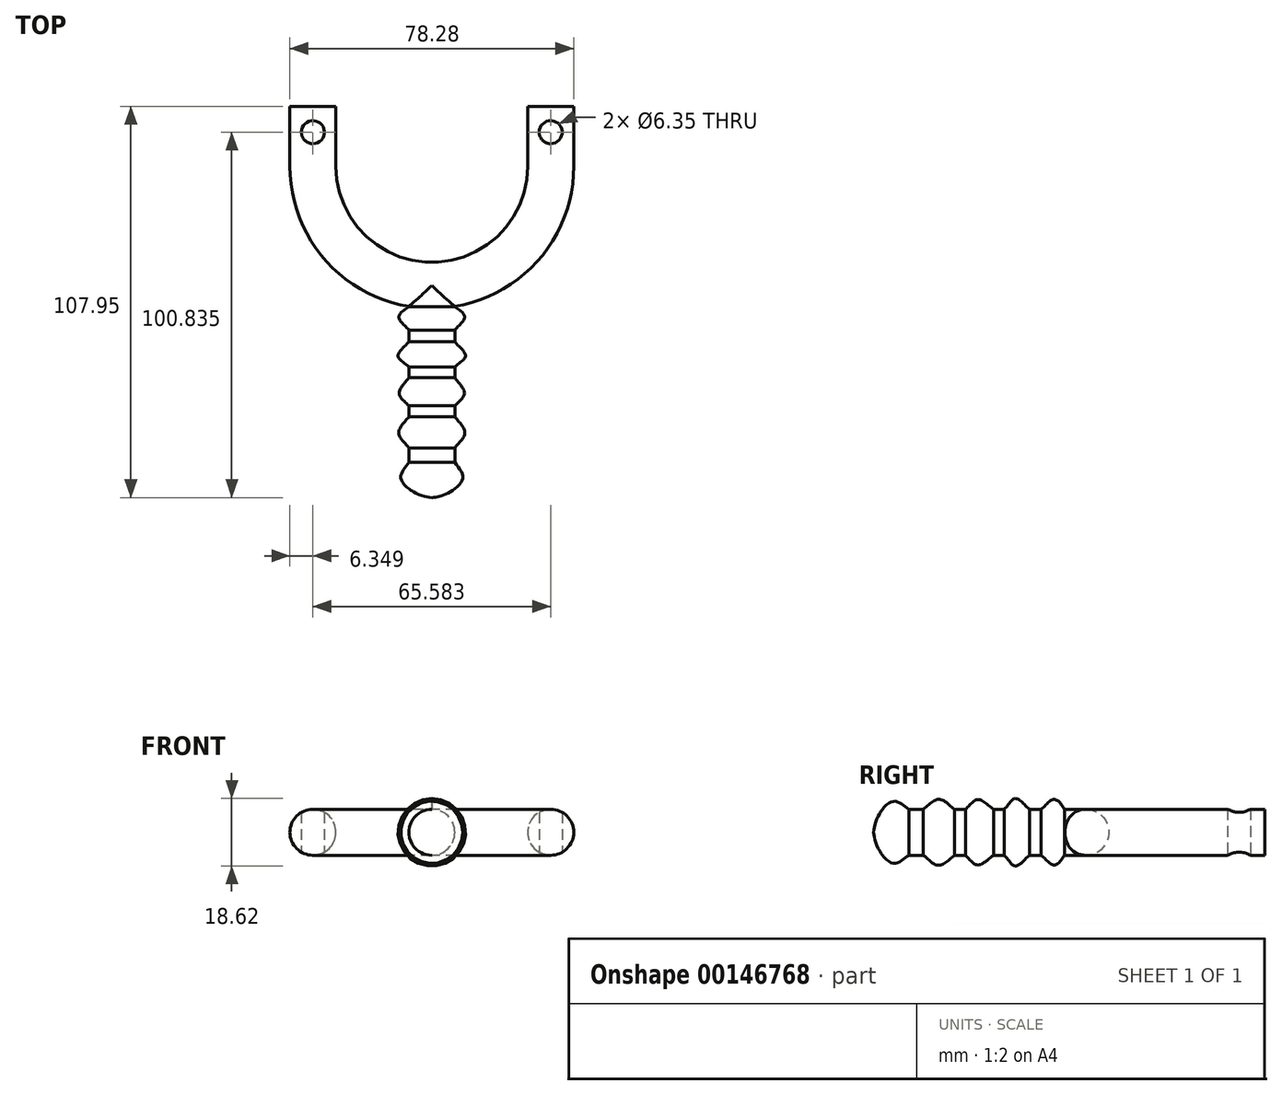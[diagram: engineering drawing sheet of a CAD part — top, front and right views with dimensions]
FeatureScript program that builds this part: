
annotation { "Feature Type Name" : "Feature", "Feature Type Description" : "" }
export const myFeature = defineFeature(function(context is Context, id is Id, definition is map)
    precondition{}
    {
        {
            var Q0;
            Q0=qCreatedBy(makeId("Top.planeOp"),FACE);
            var sketch = newSketch(context, id + "F0", { "sketchPlane" : qUnion([Q0])});
            skArc(sketch, "E0", {"start": v(-32.8, 32.8) * mm, "mid": v(-23.19, 9.6) * mm, "end": v(0, 0) * mm});
            skArc(sketch, "E1.MirrorCS", {"start": v(32.8, 32.8) * mm, "mid": v(23.19, 9.6) * mm, "end": v(0, 0) * mm});
            skLineSegment(sketch, "E2", {"start": v(-32.8, 32.8) * mm, "end": v(-32.8, 49.37) * mm});
            skLineSegment(sketch, "E3.MirrorCS", {"start": v(32.8, 32.8) * mm, "end": v(32.8, 49.37) * mm});
            skLineSegment(sketch, "E4", {"start": v(0, 0) * mm, "end": v(0, -55.64) * mm});
            skSolve(sketch);
        }
        {
            var Q0;
            Q0=qCreatedBy(makeId("Front.planeOp"),FACE);
            var sketch = newSketch(context, id + "F1", { "sketchPlane" : qUnion([Q0])});
            skCircle(sketch, "E5", {"center": v(0, 0) * mm, "radius": 6.35 * mm});
            skSolve(sketch);
        }
        {
            var Q0;
            Q0=makeQuery(id+"F1.imprint","IMPRINT",FACE,{"disambiguationData":[TD([[makeQuery(id+"F1.imprint","IMPRINT",EDGE,{"derivedFrom":sQuery(id+"F1.wireOp",EDGE,"E5")}),1.0]])]});
            var Q1;
            Q1=sQuery(id+"F0.wireOp",EDGE,"E4");
            sweep(context, id + "F2", {"profiles" : qUnion([Q0]), "path" : qUnion([Q1])});
        }
        {
            var Q0;
            Q0=qCreatedBy(makeId("Right.planeOp"),FACE);
            var sketch = newSketch(context, id + "F3", { "sketchPlane" : qUnion([Q0])});
            skCircle(sketch, "E6", {"center": v(0, 0) * mm, "radius": 6.35 * mm});
            skSolve(sketch);
        }
        {
            var Q0;
            Q0=makeQuery(id+"F3.imprint","IMPRINT",FACE,{"disambiguationData":[TD([[makeQuery(id+"F3.imprint","IMPRINT",EDGE,{"derivedFrom":sQuery(id+"F3.wireOp",EDGE,"E6")}),1.0]])]});
            var Q1;
            Q1=sQuery(id+"F0.wireOp",EDGE,"E2");
            var Q2;
            Q2=sQuery(id+"F0.wireOp",EDGE,"E0");
            sweep(context, id + "F4", {"operationType" : NewBodyOperationType.ADD, "profiles" : qUnion([Q0]), "path" : qUnion([Q1, Q2])});
        }
        {
            var Q0;
            Q0 = qSketchRegion(id + "F3", true);
            var Q1;
            Q1=sQuery(id+"F0.wireOp",EDGE,"E1.MirrorCS");
            var Q2;
            Q2=sQuery(id+"F0.wireOp",EDGE,"E3.MirrorCS");
            sweep(context, id + "F5", {"operationType" : NewBodyOperationType.ADD, "profiles" : qUnion([Q0]), "path" : qUnion([Q1, Q2])});
        }
        {
            var Q0;
            Q0=qCreatedBy(makeId("Top.planeOp"),FACE);
            var sketch = newSketch(context, id + "F6", { "sketchPlane" : qUnion([Q0])});
            skCircle(sketch, "E7", {"center": v(32.8, 42.26) * mm, "radius": 3.18 * mm});
            skCircle(sketch, "E8.MirrorC", {"center": v(-32.8, 42.26) * mm, "radius": 3.18 * mm});
            skSolve(sketch);
        }
        {
            var Q0;
            Q0 = qSketchRegion(id + "F6", true);
            extrude(context, id + "F7", {"entities" : qUnion([Q0]), "operationType" : NewBodyOperationType.REMOVE, "endBound" : BoundingType.SYMMETRIC, "depth" : 25.4 * mm});
        }
        {
            var Q0;
            Q0=qCreatedBy(makeId("Top.planeOp"),FACE);
            var sketch = newSketch(context, id + "F8", { "sketchPlane" : qUnion([Q0])});
            skFitSpline(sketch, "E9", {"points": [v(5.89, -5.61) * mm, v(9.02, -9.12) * mm, v(5.6, -14.06) * mm, v(9.3, -19.47) * mm, v(5.7, -23.65) * mm, v(9.02, -29.82) * mm, v(5.7, -34.56) * mm, v(9.12, -40.54) * mm, v(5.5, -46.62) * mm, v(8.55, -52.6) * mm, v(4.37, -57.34) * mm, v(0, -58.58) * mm], "startDerivative": vector(62.47, -38.26) * mm, "endDerivative": vector(-48.5, -4.43) * mm});
            skLineSegment(sketch, "E10", {"start": v(5.89, -5.61) * mm, "end": v(0, -5.61) * mm});
            skLineSegment(sketch, "E11", {"start": v(0, -5.61) * mm, "end": v(0, -58.58) * mm});
            skSolve(sketch);
        }
        {
            var Q0;
            Q0 = qSketchRegion(id + "F8", true);
            var Q1;
            Q1=sQuery(id+"F8.wireOp",EDGE,"E11");
            revolve(context, id + "F9", {"operationType" : NewBodyOperationType.ADD, "entities" : qUnion([Q0]), "axis" : qUnion([Q1]), "revolveType" : RevolveType.FULL});
        }
    });
